# Revit family: Emergency_Equipment-Tepid-Floor_Mounted_Eye_Face_Wash-T2510
name_source: partatom
category: Plumbing Fixtures
revit_build: Autodesk Revit Architecture 2016 (Build: 20150220_1215(x64)
units: mm (PartAtom-declared; Revit-internal decimal feet)

## family parameters
Always vertical = Yes
Cut with Voids When Loaded = No
OmniClass Number = 23.45.05.14.24
OmniClass Title = Eye Wash Fountains
Part Type = Normal
Room Calculation Point = No
Round Connector Dimension = Use Diameter
Shared = No
Work Plane-Based = No

## types (12) — shared parameters
C Pipe length = 2.5 "
CW Connection = Yes
Cold Water Connection = 1"
Description = Floor Mounted Eye-Face Wash
Dimension Disclaimer = Dimensions are ±0.50”. Design and specifications are subject to change without notice.
Drain Connection = 1"
HW Connection = Yes
Height = 38.4 "
Hot Water Connection = 1"
Length = 20.6 "
Manufacturer = Stingray Systems
Product Documentation Link = http://www.tepid.com
Product Name = Floor Mounted Standard Eye-Face Wash
Product Page URL = http://www.tepid.com
URL = www.tepid.com
Vent Connection = No
Version = 2016-v1.0a
Waste Connection = Yes

## per-type parameters (varying)
| type | AB | Base Finish | Bowl Material | Filter | Pipe Finish | Width | nab |
| T2510-EP-NFT-ABNA | Yes | Metal - Stingray - Epoxy Coated EP | Plastic - Stingray - ABS AB | No | Metal - Stingray - Epoxy Coated EP | 16.3 " | No |
| T2510-EP-NFT-SSNA | No | Metal - Stingray - Epoxy Coated EP | Metal - Stingray - Stainless Steel SS | No | Metal - Stingray - Epoxy Coated EP | 14.3 " | Yes |
| T2510-GA-NFT-ABNA | Yes | Metal - Stingray - Epoxy Coated EP | Plastic - Stingray - ABS AB | No | Metal - Stingray - Galvanized GA | 16.3 " | No |
| T2510-GA-NFT-SSNA | No | Metal - Stingray - Epoxy Coated EP | Metal - Stingray - Stainless Steel SS | No | Metal - Stingray - Galvanized GA | 14.3 " | Yes |
| T2510-SS-NFT-ABNA | Yes | Metal - Stingray - Stainless Steel SS | Plastic - Stingray - ABS AB | No | Metal - Stingray - Stainless Steel SS | 16.3 " | No |
| T2510-SS-NFT-SSNA | No | Metal - Stingray - Stainless Steel SS | Metal - Stingray - Stainless Steel SS | No | Metal - Stingray - Stainless Steel SS | 14.3 " | Yes |
| T2510-SS-FLT-SSNA | No | Metal - Stingray - Stainless Steel SS | Metal - Stingray - Stainless Steel SS | Yes | Metal - Stingray - Stainless Steel SS | 14.3 " | Yes |
| T2510-SS-FLT-ABNA | Yes | Metal - Stingray - Stainless Steel SS | Plastic - Stingray - ABS AB | Yes | Metal - Stingray - Stainless Steel SS | 16.3 " | No |
| T2510-GA-FLT-SSNA | No | Metal - Stingray - Epoxy Coated EP | Metal - Stingray - Stainless Steel SS | Yes | Metal - Stingray - Galvanized GA | 14.3 " | Yes |
| T2510-GA-FLT-ABNA | Yes | Metal - Stingray - Epoxy Coated EP | Plastic - Stingray - ABS AB | Yes | Metal - Stingray - Galvanized GA | 16.3 " | No |
| T2510-EP-FLT-SSNA | No | Metal - Stingray - Epoxy Coated EP | Metal - Stingray - Stainless Steel SS | Yes | Metal - Stingray - Epoxy Coated EP | 14.3 " | Yes |
| T2510-EP-FLT-ABNA | Yes | Metal - Stingray - Epoxy Coated EP | Plastic - Stingray - ABS AB | Yes | Metal - Stingray - Epoxy Coated EP | 16.3 " | No |

note: column(s) folded — value = type name in every type: Model

## geometry (parser evidence)
native form markers: Sweep x7
no freeform markers — native parametric forms only
